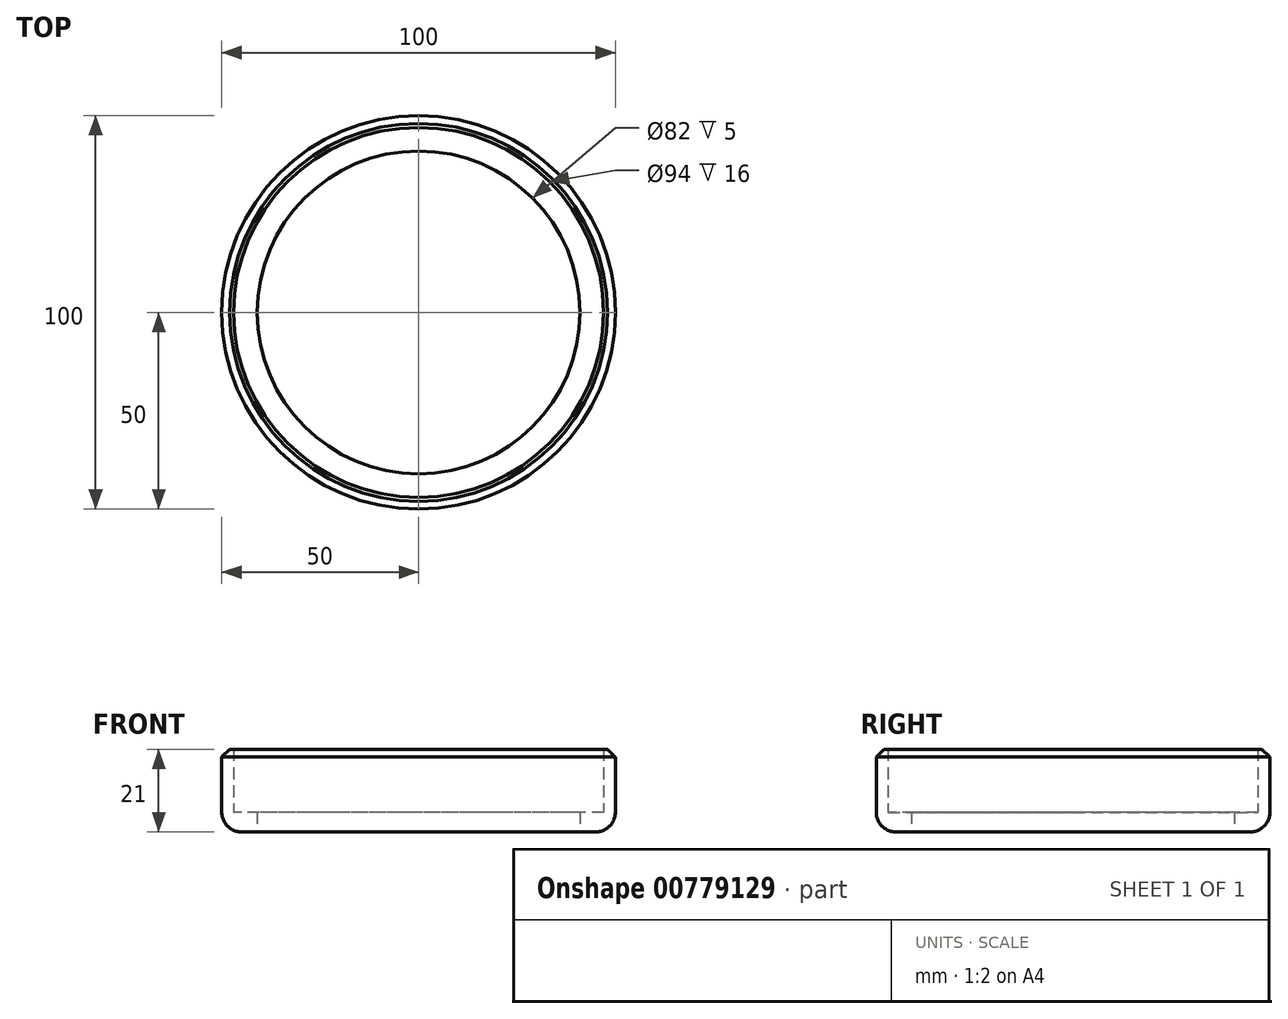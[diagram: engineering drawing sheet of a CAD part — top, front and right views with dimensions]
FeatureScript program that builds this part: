
annotation { "Feature Type Name" : "Feature", "Feature Type Description" : "" }
export const myFeature = defineFeature(function(context is Context, id is Id, definition is map)
    precondition{}
    {
        {
            var Q0;
            Q0=qCreatedBy(makeId("Top.planeOp"),FACE);
            var sketch = newSketch(context, id + "F0", { "sketchPlane" : qUnion([Q0])});
            skCircle(sketch, "E0", {"center": v(0, 0) * mm, "radius": 47.5 * mm});
            skCircle(sketch, "E1", {"center": v(0, 0) * mm, "radius": 50 * mm});
            skCircle(sketch, "E2", {"center": v(0, 0) * mm, "radius": 41 * mm});
            skSolve(sketch);
        }
        {
            var Q0;
            Q0=makeQuery(id+"F0.imprint","IMPRINT",FACE,{"disambiguationData":[TD([[makeQuery(id+"F0.imprint","IMPRINT",EDGE,{"derivedFrom":sQuery(id+"F0.wireOp",EDGE,"E0")}),1.0]])]});
            extrude(context, id + "F1", {"entities" : qUnion([Q0]), "depth" : 5 * mm, "offsetDistance" : 25 * mm});
        }
        {
            var Q0;
            Q0=qCreatedBy(makeId("Top.planeOp"),FACE);
            var sketch = newSketch(context, id + "F2", { "sketchPlane" : qUnion([Q0])});
            skCircle(sketch, "E3", {"center": v(0, 0) * mm, "radius": 50 * mm});
            skCircle(sketch, "E4", {"center": v(0, 0) * mm, "radius": 47 * mm});
            skSolve(sketch);
        }
        {
            var Q0;
            Q0=makeQuery(id+"F2.imprint","IMPRINT",FACE,{"disambiguationData":[TD([[makeQuery(id+"F2.imprint","IMPRINT",EDGE,{"derivedFrom":sQuery(id+"F2.wireOp",EDGE,"E3")}),1.0]])]});
            extrude(context, id + "F3", {"entities" : qUnion([Q0]), "operationType" : NewBodyOperationType.ADD, "depth" : 21 * mm, "offsetDistance" : 25 * mm});
        }
        {
            var Q0;
            Q0=makeQuery(id+"F3.opExtrude","CAP_EDGE",EDGE,{"disambiguationData":[OSD([sQuery(id+"F2.wireOp",EDGE,"E3")])],"isStart":true});
            fillet(context, id + "F4", {"entities" : qUnion([Q0]), "radius" : 5 * mm, "tangentPropagation" : true, "allowEdgeOverflow" : false});
        }
        {
            var Q0;
            Q0=makeQuery(id+"F3.opExtrude","CAP_EDGE",EDGE,{"disambiguationData":[OSD([sQuery(id+"F2.wireOp",EDGE,"E3")])],"isStart":false});
            chamfer(context, id + "F5", {"entities" : qUnion([Q0]), "width" : 2 * mm, "tangentPropagation" : true});
        }
    });
